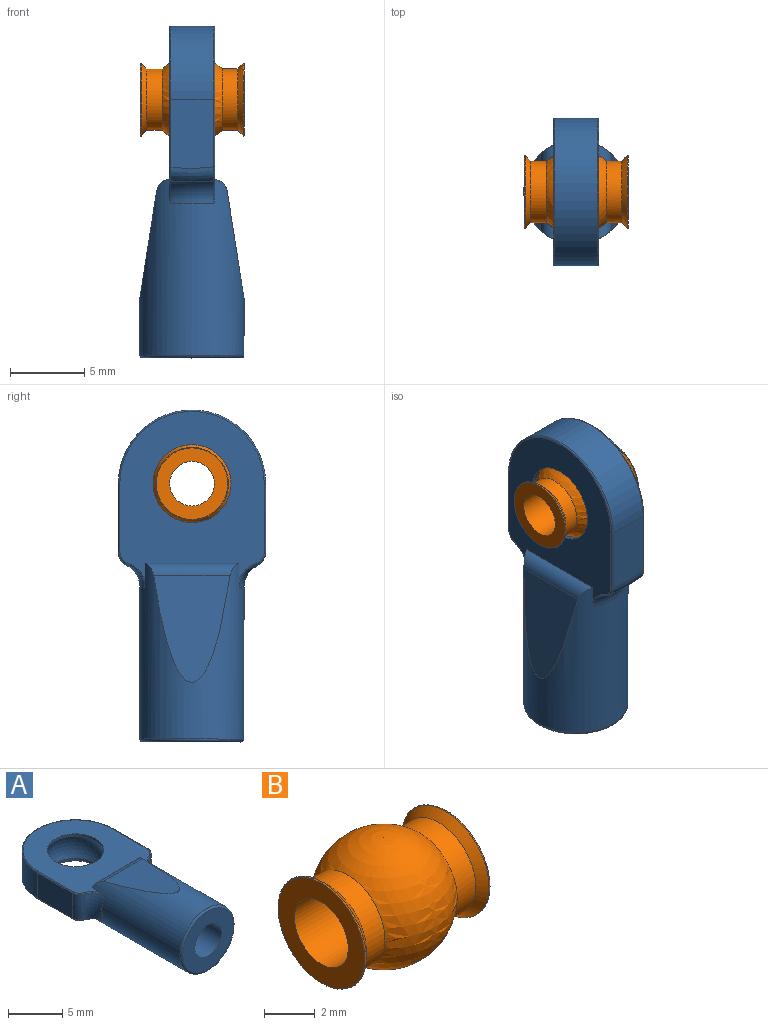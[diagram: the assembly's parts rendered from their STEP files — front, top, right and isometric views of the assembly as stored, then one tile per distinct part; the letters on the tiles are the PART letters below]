
ASSEMBLY  parts=2 mates=1
PART A: 43 faces, bbox 11x22.7x7.6 mm
  f0: sphere r=2.9mm, area 45.3mm2, adj f1,f42
  f1: cylinder r=2.62mm len=5.24mm, axis (0,0,1), area 4.7mm2, adj f0,f41
  f2: cylinder r=1.75mm len=9mm, axis (0,1,0), area 99mm2, adj f3,f34
  f3: plane 3.5x3.5mm, normal (0,-1,0), area 9.6mm2, adj f2
  f4: bspline ~1.59x1.21mm, area 0.2mm2, adj f10,f13,f33,f41
  f5: bspline ~0.16x0.11mm, area 0mm2, adj f6,f10,f15,f41
  f6: cylinder r=0.1mm len=4.51mm, axis (0,-1,0), area 0.7mm2, adj f5,f7,f16,f41
  f7: torus R=4.85mm, axis (0,0,-1), area 2.4mm2, adj f6,f8,f17,f41
  f8: cylinder r=0.1mm len=4.51mm, axis (0,1,0), area 0.7mm2, adj f7,f9,f18,f41
  f9: bspline ~0.16x0.11mm, area 0mm2, adj f8,f12,f19,f41
  f10: bspline ~0.81x0.68mm, area 0.2mm2, adj f4,f5,f14,f41
  f11: bspline ~1.59x1.21mm, area 0.2mm2, adj f12,f21,f33,f41
  f12: bspline ~0.81x0.68mm, area 0.2mm2, adj f9,f11,f20,f41
  f13: torus R=5.1mm, axis (0,1,0), area 5.3mm2, adj f4,f14,f22,f33
  f14: bspline ~3.06x1mm, area 3.3mm2, adj f10,f13,f15,f16,f28,f39
  f15: extruded ~0.16x0.04mm, area 0mm2, adj f5,f14,f16
  f16: plane 4.62x2.86mm, normal (1,0,0), area 13.1mm2, adj f6,f14,f15,f17,f24,f39
  f17: cylinder r=4.95mm len=9.9mm, axis (0,0,1), area 44.5mm2, adj f7,f16,f18,f25
  f18: plane 4.62x2.86mm, normal (-1,0,0), area 13.1mm2, adj f8,f17,f19,f20,f26,f40
  f19: extruded ~0.16x0.04mm, area 0mm2, adj f9,f18,f20
  f20: bspline ~3.06x1mm, area 3.3mm2, adj f12,f18,f19,f21,f30,f40
  f21: torus R=5.1mm, axis (0,1,0), area 5.3mm2, adj f11,f20,f29,f33
  f22: bspline ~1.59x1.21mm, area 0.2mm2, adj f13,f28,f31,f33
  f23: bspline ~0.16x0.11mm, area 0mm2, adj f24,f28,f31,f39
  f24: cylinder r=0.1mm len=4.51mm, axis (0,1,0), area 0.7mm2, adj f16,f23,f25,f31
  f25: torus R=4.85mm, axis (0,0,1), area 2.4mm2, adj f17,f24,f26,f31
  f26: cylinder r=0.1mm len=4.51mm, axis (0,-1,0), area 0.7mm2, adj f18,f25,f27,f31
  f27: bspline ~0.16x0.11mm, area 0mm2, adj f26,f30,f31,f40
  f28: bspline ~0.81x0.68mm, area 0.2mm2, adj f14,f22,f23,f31
  f29: bspline ~1.59x1.21mm, area 0.2mm2, adj f21,f30,f31,f33
  f30: bspline ~0.81x0.68mm, area 0.2mm2, adj f20,f27,f29,f31
  f31: plane 11.36x9.7mm, normal (0,0,1), area 67.9mm2, adj f22,f23,f24,f25,f26,f27,f28,f29
  f32: torus R=3.3mm, axis (0,-1,0), area 6.8mm2, adj f33,f34
  f33: cylinder r=3.5mm len=11.8mm, axis (0,-1,0), area 183.7mm2, adj f4,f11,f13,f21,f22,f29,f31,f32
  f34: plane 6.6x6.6mm, normal (0,-1,0), area 24.6mm2, adj f2,f32
  f35: cylinder r=1mm len=6.3mm, axis (-1,0,0), area 7.3mm2, adj f33,f36,f41
  f36: plane 7.16x5.13mm, normal (0,0.15,-0.99), area 25.7mm2, adj f33,f35
  f37: cylinder r=1mm len=6.3mm, axis (1,0,0), area 7.3mm2, adj f31,f33,f38
  f38: plane 7.16x5.13mm, normal (0,0.15,0.99), area 25.7mm2, adj f33,f37
  f39: extruded ~0.16x0.04mm, area 0mm2, adj f14,f16,f23
  f40: extruded ~0.16x0.04mm, area 0mm2, adj f18,f20,f27
  f41: plane 11.36x9.7mm, normal (0,0,-1), area 67.9mm2, adj f1,f4,f5,f6,f7,f8,f9,f10
  f42: cylinder r=2.62mm len=5.24mm, axis (0,0,1), area 4.7mm2, adj f0,f31
PART B: 10 faces, bbox 7x5.8x5.8 mm
  f0: torus R=2.4mm, axis (1,0,0), area 1.4mm2, adj f1,f2
  f1: cone r=2.28mm half-angle=45deg, axis (1,0,0), area 7.3mm2, adj f0,f8
  f2: plane 4.81x4.81mm, normal (1,0,0), area 11.1mm2, adj f0,f9
  f3: torus R=2.4mm, axis (1,0,0), area 1.4mm2, adj f4,f5
  f4: plane 4.81x4.81mm, normal (-1,0,0), area 11.1mm2, adj f3,f9
  f5: cone r=2.28mm half-angle=45deg, axis (-1,0,0), area 7.3mm2, adj f3,f6
  f6: cylinder r=2.06mm len=4.13mm, axis (1,0,0), area 13.5mm2, adj f5,f7
  f7: sphere r=2.88mm, area 73mm2, adj f6,f8
  f8: cylinder r=2.06mm len=4.13mm, axis (1,0,0), area 13.5mm2, adj f1,f7
  f9: cylinder r=1.5mm len=6.98mm, axis (1,0,0), area 65.8mm2, adj f2,f4
PLACE A rot(axis=(0.58,0.58,0.58),120deg) t=(7.59,-1.77,-0.3)mm
PLACE B rot(axis=(1,0,0),0.1deg) t=(7.61,-1.77,-0.3)mm
MATE fastened B.f0 <-> A.f1  axis (1,0,0) through (11.1,-1.77,-0.3)mm
